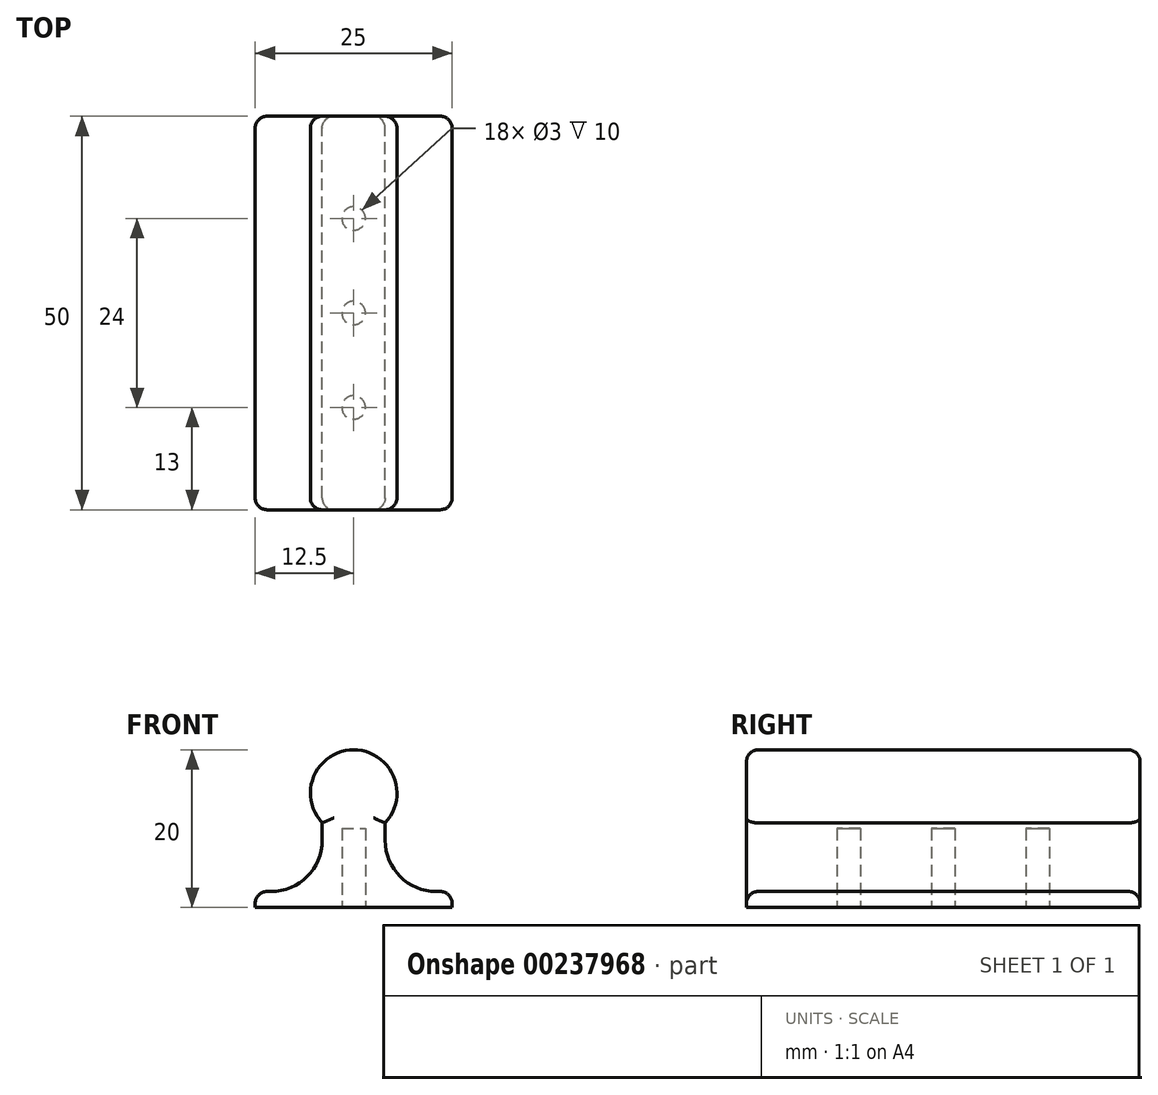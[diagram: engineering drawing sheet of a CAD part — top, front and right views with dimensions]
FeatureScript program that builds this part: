
annotation { "Feature Type Name" : "Feature", "Feature Type Description" : "" }
export const myFeature = defineFeature(function(context is Context, id is Id, definition is map)
    precondition{}
    {
        {
            var Q0;
            Q0=qCreatedBy(makeId("Front.planeOp"),FACE);
            var sketch = newSketch(context, id + "F0", { "sketchPlane" : qUnion([Q0])});
            skLineSegment(sketch, "E0", {"start": v(-12.5, 0) * mm, "end": v(12.5, 0) * mm});
            skLineSegment(sketch, "E1", {"start": v(-12.5, 0) * mm, "end": v(-12.5, 2) * mm});
            skLineSegment(sketch, "E2", {"start": v(12.5, 0) * mm, "end": v(12.5, 2) * mm});
            skLineSegment(sketch, "E3", {"start": v(-12.5, 2) * mm, "end": v(-10.5, 2) * mm});
            skLineSegment(sketch, "E4", {"start": v(12.5, 2) * mm, "end": v(10.5, 2) * mm});
            skLineSegment(sketch, "E5", {"start": v(-4, 10.73) * mm, "end": v(-4, 8.5) * mm});
            skLineSegment(sketch, "E6", {"start": v(4, 10.73) * mm, "end": v(4, 8.5) * mm});
            skArc(sketch, "E7", {"start": v(4, 10.73) * mm, "mid": v(0, 20) * mm, "end": v(-4, 10.73) * mm});
            skPoint(sketch, "E8.visualSharp", {"position": v(4, 2) * mm});
            skArc(sketch, "E8.filletArc", {"start": v(4, 8.5) * mm, "mid": v(5.9, 3.9) * mm, "end": v(10.5, 2) * mm});
            skPoint(sketch, "E9.visualSharp", {"position": v(-4, 2) * mm});
            skArc(sketch, "E9.filletArc", {"start": v(-10.5, 2) * mm, "mid": v(-5.9, 3.9) * mm, "end": v(-4, 8.5) * mm});
            skSolve(sketch);
        }
        {
            var Q0;
            Q0 = qSketchRegion(id + "F0", true);
            extrude(context, id + "F1", {"entities" : qUnion([Q0]), "depth" : 50 * mm, "symmetric" : true});
        }
        {
            var Q0;
            Q0=makeQuery(id+"F1.opExtrude","SWEPT_EDGE",EDGE,{"disambiguationData":[OSD([sQuery(id+"F0.wireOp",EDGE,"E2"),sQuery(id+"F0.wireOp",EDGE,"E4")])]});
            var Q1;
            Q1=makeQuery(id+"F1.opExtrude","SWEPT_EDGE",EDGE,{"disambiguationData":[OSD([sQuery(id+"F0.wireOp",EDGE,"E1"),sQuery(id+"F0.wireOp",EDGE,"E3")])]});
            fillet(context, id + "F2", {"entities" : qUnion([Q0, Q1]), "radius" : 1.5 * mm, "tangentPropagation" : true, "allowEdgeOverflow" : false});
        }
        {
            var Q0;
            Q0=makeQuery(id+"F1.opExtrude","CAP_EDGE",EDGE,{"disambiguationData":[OSD([sQuery(id+"F0.wireOp",EDGE,"E7")])],"isStart":false});
            var Q1;
            Q1=makeQuery(id+"F1.opExtrude","CAP_EDGE",EDGE,{"disambiguationData":[OSD([sQuery(id+"F0.wireOp",EDGE,"E6")])],"isStart":false});
            var Q2;
            Q2=makeQuery(id+"F1.opExtrude","CAP_EDGE",EDGE,{"disambiguationData":[OSD([sQuery(id+"F0.wireOp",EDGE,"E5")])],"isStart":false});
            var Q3;
            Q3=makeQuery(id+"F1.opExtrude","CAP_EDGE",EDGE,{"disambiguationData":[OSD([sQuery(id+"F0.wireOp",EDGE,"E7")])],"isStart":true});
            var Q4;
            Q4=makeQuery(id+"F1.opExtrude","CAP_EDGE",EDGE,{"disambiguationData":[OSD([sQuery(id+"F0.wireOp",EDGE,"E6")])],"isStart":true});
            var Q5;
            Q5=makeQuery(id+"F1.opExtrude","CAP_EDGE",EDGE,{"disambiguationData":[OSD([sQuery(id+"F0.wireOp",EDGE,"E9.filletArc")])],"isStart":true});
            fillet(context, id + "F3", {"entities" : qUnion([Q0, Q1, Q2, Q3, Q4, Q5]), "radius" : 1.5 * mm, "tangentPropagation" : true, "allowEdgeOverflow" : false});
        }
        {
            var Q0;
            Q0=makeQuery(id+"F1.opExtrude","SWEPT_FACE",FACE,{"disambiguationData":[OSD([sQuery(id+"F0.wireOp",EDGE,"E0")])]});
            var sketch = newSketch(context, id + "F4", { "sketchPlane" : qUnion([Q0])});
            skCircle(sketch, "E10", {"center": v(0, 0) * mm, "radius": 1.5 * mm});
            skCircle(sketch, "E11", {"center": v(0, 12) * mm, "radius": 1.5 * mm});
            skCircle(sketch, "E12", {"center": v(0, -12) * mm, "radius": 1.5 * mm});
            skSolve(sketch);
        }
        {
            var Q0;
            Q0 = qSketchRegion(id + "F4", true);
            extrude(context, id + "F5", {"entities" : qUnion([Q0]), "operationType" : NewBodyOperationType.REMOVE, "oppositeDirection" : true, "depth" : 10 * mm});
        }
    });
